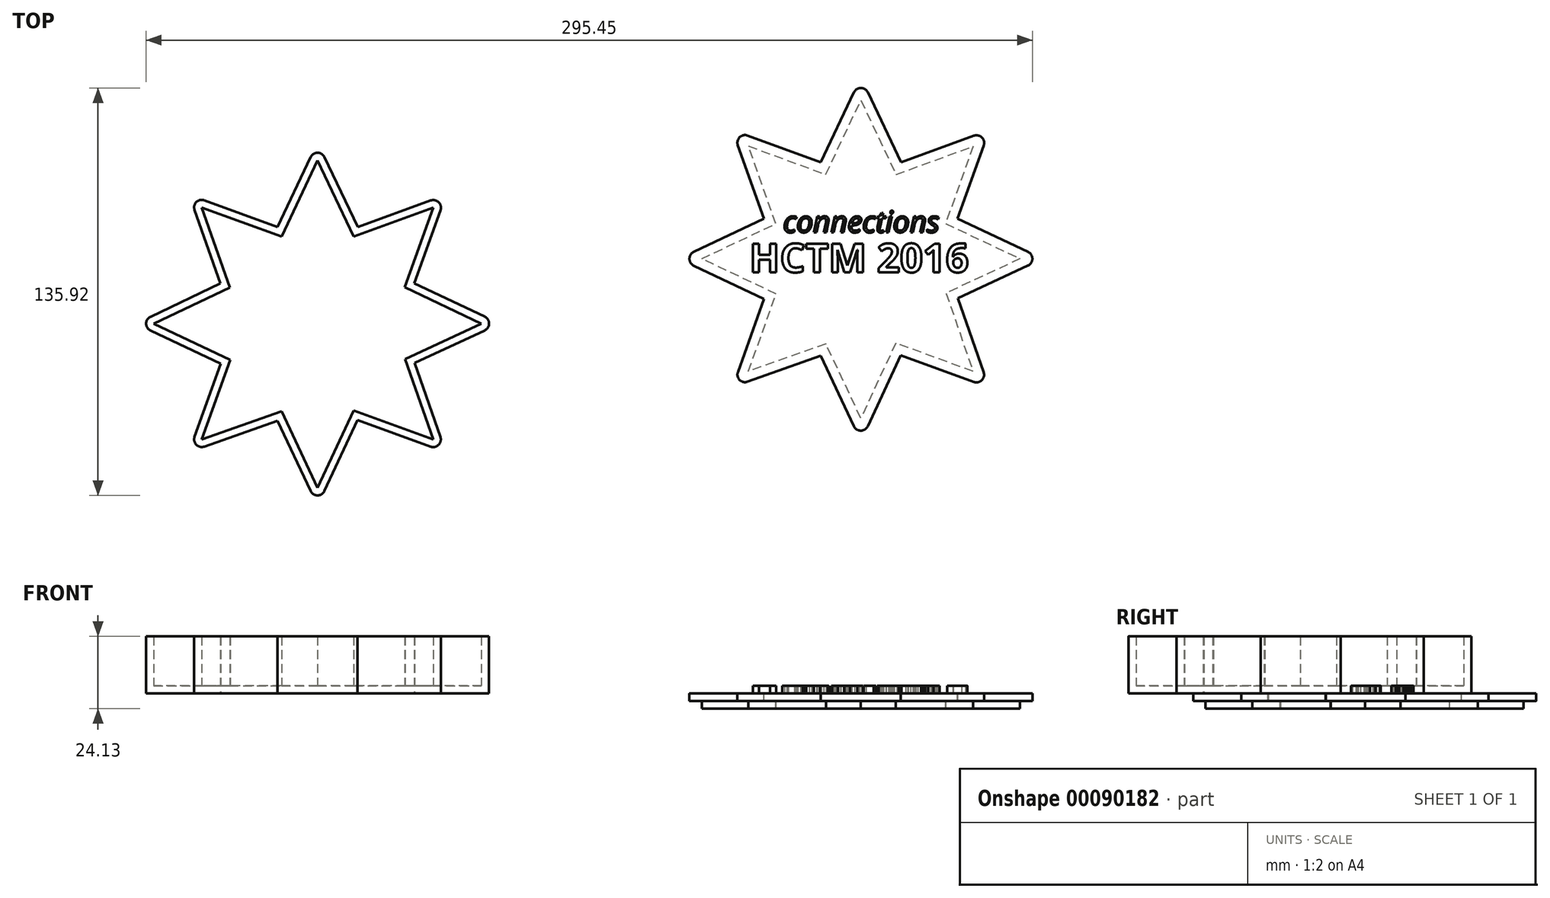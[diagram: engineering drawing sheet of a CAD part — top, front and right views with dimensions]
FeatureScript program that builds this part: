
annotation { "Feature Type Name" : "Feature", "Feature Type Description" : "" }
export const myFeature = defineFeature(function(context is Context, id is Id, definition is map)
    precondition{}
    {
        {
            var Q0;
            Q0=qCreatedBy(makeId("Top.planeOp"),FACE);
            var sketch = newSketch(context, id + "F0", { "sketchPlane" : qUnion([Q0])});
            skLineSegment(sketch, "E0", {"start": v(0, 60.39) * mm, "end": v(13.37, 32.16) * mm});
            skLineSegment(sketch, "E1", {"start": v(13.37, 32.16) * mm, "end": v(42.8, 42.9) * mm});
            skLineSegment(sketch, "E2", {"start": v(42.8, 42.9) * mm, "end": v(32.23, 13.42) * mm});
            skLineSegment(sketch, "E3", {"start": v(32.23, 13.42) * mm, "end": v(60.6, 0) * mm});
            skLineSegment(sketch, "E4", {"start": v(60.6, 0) * mm, "end": v(32.38, -13.15) * mm});
            skLineSegment(sketch, "E5", {"start": v(32.38, -13.15) * mm, "end": v(42.67, -42.9) * mm});
            skLineSegment(sketch, "E6", {"start": v(42.67, -42.9) * mm, "end": v(13.29, -32.15) * mm});
            skLineSegment(sketch, "E7", {"start": v(13.29, -32.15) * mm, "end": v(0, -60.78) * mm});
            skLineSegment(sketch, "E8", {"start": v(0, -60.78) * mm, "end": v(-13.33, -32.37) * mm});
            skLineSegment(sketch, "E9", {"start": v(-13.33, -32.37) * mm, "end": v(-42.81, -42.8) * mm});
            skLineSegment(sketch, "E10", {"start": v(-42.81, -42.8) * mm, "end": v(-32.26, -13.38) * mm});
            skLineSegment(sketch, "E11", {"start": v(-32.26, -13.38) * mm, "end": v(-60.56, 0) * mm});
            skLineSegment(sketch, "E12", {"start": v(-60.56, 0) * mm, "end": v(-32.38, 13.38) * mm});
            skLineSegment(sketch, "E13", {"start": v(-32.38, 13.38) * mm, "end": v(-42.81, 42.98) * mm});
            skLineSegment(sketch, "E14", {"start": v(-42.81, 42.98) * mm, "end": v(-13.33, 32.19) * mm});
            skLineSegment(sketch, "E15", {"start": v(-13.33, 32.19) * mm, "end": v(0, 60.39) * mm});
            skLineSegment(sketch, "E16", {"start": v(181.12, 82) * mm, "end": v(194.5, 53.77) * mm});
            skLineSegment(sketch, "E17", {"start": v(194.5, 53.77) * mm, "end": v(223.91, 64.5) * mm});
            skLineSegment(sketch, "E18", {"start": v(223.91, 64.5) * mm, "end": v(213.35, 35.03) * mm});
            skLineSegment(sketch, "E19", {"start": v(213.35, 35.03) * mm, "end": v(241.72, 21.61) * mm});
            skLineSegment(sketch, "E20", {"start": v(241.72, 21.61) * mm, "end": v(213.5, 8.46) * mm});
            skLineSegment(sketch, "E21", {"start": v(213.5, 8.46) * mm, "end": v(223.8, -21.3) * mm});
            skLineSegment(sketch, "E22", {"start": v(223.8, -21.3) * mm, "end": v(194.4, -10.53) * mm});
            skLineSegment(sketch, "E23", {"start": v(194.4, -10.53) * mm, "end": v(181.12, -39.17) * mm});
            skLineSegment(sketch, "E24", {"start": v(181.12, -39.17) * mm, "end": v(167.78, -10.76) * mm});
            skLineSegment(sketch, "E25", {"start": v(167.78, -10.76) * mm, "end": v(138.3, -21.2) * mm});
            skLineSegment(sketch, "E26", {"start": v(138.3, -21.2) * mm, "end": v(148.86, 8.23) * mm});
            skLineSegment(sketch, "E27", {"start": v(148.86, 8.23) * mm, "end": v(120.56, 21.61) * mm});
            skLineSegment(sketch, "E28", {"start": v(120.56, 21.61) * mm, "end": v(148.74, 35) * mm});
            skLineSegment(sketch, "E29", {"start": v(148.74, 35) * mm, "end": v(138.3, 64.59) * mm});
            skLineSegment(sketch, "E30", {"start": v(138.3, 64.59) * mm, "end": v(167.78, 53.8) * mm});
            skLineSegment(sketch, "E31", {"start": v(167.78, 53.8) * mm, "end": v(181.12, 82) * mm});
            skLineSegment(sketch, "E32.0", {"start": v(169.44, 49.77) * mm, "end": v(181.12, 74.49) * mm});
            skLineSegment(sketch, "E32.1", {"start": v(143.6, 59.23) * mm, "end": v(169.44, 49.77) * mm});
            skLineSegment(sketch, "E32.2", {"start": v(152.74, 33.33) * mm, "end": v(143.6, 59.23) * mm});
            skLineSegment(sketch, "E32.3", {"start": v(128.07, 21.62) * mm, "end": v(152.74, 33.33) * mm});
            skLineSegment(sketch, "E32.4", {"start": v(152.87, 9.89) * mm, "end": v(128.07, 21.62) * mm});
            skLineSegment(sketch, "E32.5", {"start": v(234.16, 21.63) * mm, "end": v(209.51, 10.15) * mm});
            skLineSegment(sketch, "E32.6", {"start": v(209.34, 33.37) * mm, "end": v(234.16, 21.63) * mm});
            skLineSegment(sketch, "E32.7", {"start": v(218.57, 59.14) * mm, "end": v(209.34, 33.37) * mm});
            skLineSegment(sketch, "E32.8", {"start": v(192.84, 49.74) * mm, "end": v(218.57, 59.14) * mm});
            skLineSegment(sketch, "E32.9", {"start": v(209.51, 10.15) * mm, "end": v(218.54, -15.95) * mm});
            skLineSegment(sketch, "E32.10", {"start": v(218.54, -15.95) * mm, "end": v(192.73, -6.5) * mm});
            skLineSegment(sketch, "E32.11", {"start": v(192.73, -6.5) * mm, "end": v(181.1, -31.57) * mm});
            skLineSegment(sketch, "E32.12", {"start": v(181.1, -31.57) * mm, "end": v(169.46, -6.76) * mm});
            skLineSegment(sketch, "E32.13", {"start": v(169.46, -6.76) * mm, "end": v(143.62, -15.9) * mm});
            skLineSegment(sketch, "E32.14", {"start": v(181.12, 74.49) * mm, "end": v(192.84, 49.74) * mm});
            skLineSegment(sketch, "E32.15", {"start": v(143.62, -15.9) * mm, "end": v(152.87, 9.89) * mm});
            skSolve(sketch);
        }
        {
            var Q0;
            Q0=makeQuery(id+"F0.imprint","IMPRINT",FACE,{"disambiguationData":[TD([[makeQuery(id+"F0.imprint","IMPRINT",EDGE,{"derivedFrom":sQuery(id+"F0.wireOp",EDGE,"E32.0")}),-1.0]])]});
            extrude(context, id + "F1", {"entities" : qUnion([Q0]), "oppositeDirection" : true, "depth" : 5.08 * mm});
        }
        {
            var Q0;
            Q0=makeQuery(id+"F0.imprint","IMPRINT",FACE,{"disambiguationData":[TD([[makeQuery(id+"F0.imprint","IMPRINT",EDGE,{"derivedFrom":sQuery(id+"F0.wireOp",EDGE,"E16")}),-1.0]])]});
            extrude(context, id + "F2", {"entities" : qUnion([Q0]), "operationType" : NewBodyOperationType.ADD, "oppositeDirection" : true, "depth" : 2.54 * mm});
        }
        {
            var Q0;
            Q0=makeQuery(id+"F0.imprint","IMPRINT",FACE,{"disambiguationData":[TD([[makeQuery(id+"F0.imprint","IMPRINT",EDGE,{"derivedFrom":sQuery(id+"F0.wireOp",EDGE,"E0")}),-1.0]])]});
            extrude(context, id + "F3", {"entities" : qUnion([Q0]), "depth" : 19.05 * mm});
        }
        {
            var Q0;
            Q0=makeQuery(id+"F3.opExtrude","CAP_FACE",FACE,{"disambiguationData":[OSD([sQuery(id+"F0.wireOp",EDGE,"E0"),sQuery(id+"F0.wireOp",EDGE,"E1"),sQuery(id+"F0.wireOp",EDGE,"E2"),sQuery(id+"F0.wireOp",EDGE,"E3"),sQuery(id+"F0.wireOp",EDGE,"E4"),sQuery(id+"F0.wireOp",EDGE,"E5"),sQuery(id+"F0.wireOp",EDGE,"E6"),sQuery(id+"F0.wireOp",EDGE,"E7"),sQuery(id+"F0.wireOp",EDGE,"E8"),sQuery(id+"F0.wireOp",EDGE,"E9"),sQuery(id+"F0.wireOp",EDGE,"E10"),sQuery(id+"F0.wireOp",EDGE,"E11"),sQuery(id+"F0.wireOp",EDGE,"E12"),sQuery(id+"F0.wireOp",EDGE,"E13"),sQuery(id+"F0.wireOp",EDGE,"E14"),sQuery(id+"F0.wireOp",EDGE,"E15")])],"isStart":false});
            shell(context, id + "F4", {"entities" : qUnion([Q0]), "thickness" : 2.54 * mm});
        }
        {
            var Q0;
            Q0=makeQuery(id+"F2.opExtrude","SWEPT_EDGE",EDGE,{"disambiguationData":[OSD([sQuery(id+"F0.wireOp",EDGE,"E21"),sQuery(id+"F0.wireOp",EDGE,"E22")])]});
            var Q1;
            Q1=makeQuery(id+"F2.opExtrude","SWEPT_EDGE",EDGE,{"disambiguationData":[OSD([sQuery(id+"F0.wireOp",EDGE,"E23"),sQuery(id+"F0.wireOp",EDGE,"E24")])]});
            var Q2;
            Q2=makeQuery(id+"F2.opExtrude","SWEPT_EDGE",EDGE,{"disambiguationData":[OSD([sQuery(id+"F0.wireOp",EDGE,"E19"),sQuery(id+"F0.wireOp",EDGE,"E20")])]});
            var Q3;
            Q3=makeQuery(id+"F2.opExtrude","SWEPT_EDGE",EDGE,{"disambiguationData":[OSD([sQuery(id+"F0.wireOp",EDGE,"E17"),sQuery(id+"F0.wireOp",EDGE,"E18")])]});
            var Q4;
            Q4=makeQuery(id+"F2.opExtrude","SWEPT_EDGE",EDGE,{"disambiguationData":[OSD([sQuery(id+"F0.wireOp",EDGE,"E16"),sQuery(id+"F0.wireOp",EDGE,"E31")])]});
            var Q5;
            Q5=makeQuery(id+"F2.opExtrude","SWEPT_EDGE",EDGE,{"disambiguationData":[OSD([sQuery(id+"F0.wireOp",EDGE,"E25"),sQuery(id+"F0.wireOp",EDGE,"E26")])]});
            var Q6;
            Q6=makeQuery(id+"F2.opExtrude","SWEPT_EDGE",EDGE,{"disambiguationData":[OSD([sQuery(id+"F0.wireOp",EDGE,"E27"),sQuery(id+"F0.wireOp",EDGE,"E28")])]});
            var Q7;
            Q7=makeQuery(id+"F2.opExtrude","SWEPT_EDGE",EDGE,{"disambiguationData":[OSD([sQuery(id+"F0.wireOp",EDGE,"E29"),sQuery(id+"F0.wireOp",EDGE,"E30")])]});
            var Q8;
            Q8=makeQuery(id+"F3.opExtrude","SWEPT_EDGE",EDGE,{"disambiguationData":[OSD([sQuery(id+"F0.wireOp",EDGE,"E3"),sQuery(id+"F0.wireOp",EDGE,"E4")])]});
            var Q9;
            Q9=makeQuery(id+"F3.opExtrude","SWEPT_EDGE",EDGE,{"disambiguationData":[OSD([sQuery(id+"F0.wireOp",EDGE,"E5"),sQuery(id+"F0.wireOp",EDGE,"E6")])]});
            var Q10;
            Q10=makeQuery(id+"F3.opExtrude","SWEPT_EDGE",EDGE,{"disambiguationData":[OSD([sQuery(id+"F0.wireOp",EDGE,"E7"),sQuery(id+"F0.wireOp",EDGE,"E8")])]});
            var Q11;
            Q11=makeQuery(id+"F3.opExtrude","SWEPT_EDGE",EDGE,{"disambiguationData":[OSD([sQuery(id+"F0.wireOp",EDGE,"E9"),sQuery(id+"F0.wireOp",EDGE,"E10")])]});
            var Q12;
            Q12=makeQuery(id+"F3.opExtrude","SWEPT_EDGE",EDGE,{"disambiguationData":[OSD([sQuery(id+"F0.wireOp",EDGE,"E11"),sQuery(id+"F0.wireOp",EDGE,"E12")])]});
            var Q13;
            Q13=makeQuery(id+"F3.opExtrude","SWEPT_EDGE",EDGE,{"disambiguationData":[OSD([sQuery(id+"F0.wireOp",EDGE,"E13"),sQuery(id+"F0.wireOp",EDGE,"E14")])]});
            var Q14;
            Q14=makeQuery(id+"F3.opExtrude","SWEPT_EDGE",EDGE,{"disambiguationData":[OSD([sQuery(id+"F0.wireOp",EDGE,"E1"),sQuery(id+"F0.wireOp",EDGE,"E2")])]});
            var Q15;
            Q15=makeQuery(id+"F3.opExtrude","SWEPT_EDGE",EDGE,{"disambiguationData":[OSD([sQuery(id+"F0.wireOp",EDGE,"E0"),sQuery(id+"F0.wireOp",EDGE,"E15")])]});
            fillet(context, id + "F5", {"entities" : qUnion([Q0, Q1, Q2, Q3, Q4, Q5, Q6, Q7, Q8, Q9, Q10, Q11, Q12, Q13, Q14, Q15]), "radius" : 2.54 * mm, "tangentPropagation" : true, "allowEdgeOverflow" : false});
        }
        {
            var Q0;
            Q0=makeQuery(id+"F0.imprint","IMPRINT",FACE,{"disambiguationData":[TD([[makeQuery(id+"F0.imprint","IMPRINT",EDGE,{"derivedFrom":sQuery(id+"F0.wireOp",EDGE,"E32.0")}),-1.0]])]});
            var sketch = newSketch(context, id + "F6", { "sketchPlane" : qUnion([Q0])});
            skText(sketch, "E33", { "text": "connections", "fontName": "OpenSans-Italic.ttf"});
            skText(sketch, "E34", { "text": "HCTM 2016", "fontName": "OpenSans-Bold.ttf"});
            const initialGuessF6  = {"E33": [0.15517, 0.03042, 1, 0, 0.00715], "E34": [0.14386, 0.01711, 1, 0, 0.00964]};
            skSetInitialGuess(sketch, initialGuessF6);
            skSolve(sketch);
        }
        {
            var Q0;
            Q0 = qSketchRegion(id + "F6", true);
            extrude(context, id + "F7", {"entities" : qUnion([Q0]), "operationType" : NewBodyOperationType.ADD, "depth" : 2.54 * mm});
        }
    });
